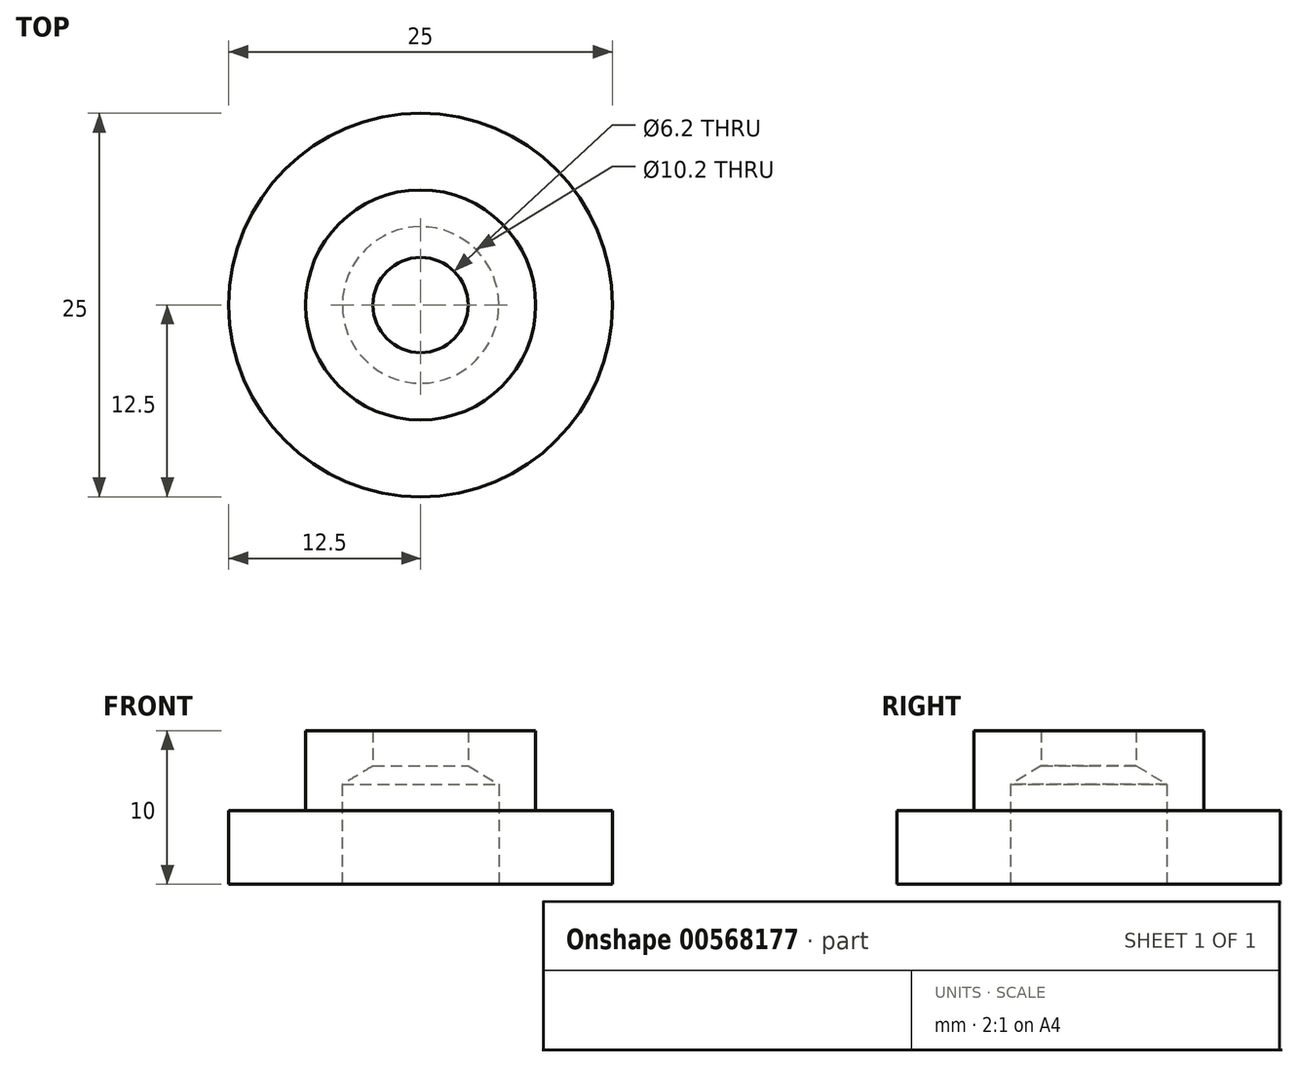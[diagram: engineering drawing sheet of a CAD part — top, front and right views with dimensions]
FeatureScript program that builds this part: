
annotation { "Feature Type Name" : "Feature", "Feature Type Description" : "" }
export const myFeature = defineFeature(function(context is Context, id is Id, definition is map)
    precondition{}
    {
        {
            var Q0;
            Q0=qCreatedBy(makeId("Top.planeOp"),FACE);
            var sketch = newSketch(context, id + "F0", { "sketchPlane" : qUnion([Q0])});
            skCircle(sketch, "E0", {"center": v(0, 0) * mm, "radius": 12.5 * mm});
            skCircle(sketch, "E1", {"center": v(0, 0) * mm, "radius": 7.5 * mm});
            skSolve(sketch);
        }
        {
            var Q0;
            Q0=makeQuery(id+"F0.imprint","IMPRINT",FACE,{"disambiguationData":[TD([[makeQuery(id+"F0.imprint","IMPRINT",EDGE,{"derivedFrom":sQuery(id+"F0.wireOp",EDGE,"E1")}),1.0]])]});
            extrude(context, id + "F1", {"entities" : qUnion([Q0]), "depth" : 10 * mm, "offsetDistance" : 25 * mm});
        }
        {
            var Q0;
            Q0=makeQuery(id+"F0.imprint","IMPRINT",FACE,{"disambiguationData":[TD([[makeQuery(id+"F0.imprint","IMPRINT",EDGE,{"derivedFrom":sQuery(id+"F0.wireOp",EDGE,"E0")}),1.0]])]});
            extrude(context, id + "F2", {"entities" : qUnion([Q0]), "operationType" : NewBodyOperationType.ADD, "depth" : 4.8 * mm, "offsetDistance" : 25 * mm});
        }
        {
            var Q0;
            Q0=sQuery(id+"F0.wireOp",VERTEX,"E0.center");
            var Q1;
            Q1=makeQuery(id+"F1.opExtrude","SWEPT_BODY",BODY,{"disambiguationData":[OSD([sQuery(id+"F0.wireOp",EDGE,"E1")])]});
            hole(context, id + "F3", {"style" : HoleStyle.SIMPLE, "endStyle" : HoleEndStyle.BLIND, "oppositeDirection" : true, "holeDiameter" : 6.2 * mm, "holeDepth" : 10 * mm, "isTappedThrough" : true, "tappedDepth" : 12 * mm, "tapClearance" : 3, "locations" : qUnion([Q0]), "scope" : qUnion([Q1])});
        }
        {
            var Q0;
            Q0=sQuery(id+"F0.wireOp",VERTEX,"E0.center");
            var Q1;
            Q1=makeQuery(id+"F1.opExtrude","SWEPT_BODY",BODY,{"disambiguationData":[OSD([sQuery(id+"F0.wireOp",EDGE,"E1")])]});
            hole(context, id + "F4", {"style" : HoleStyle.SIMPLE, "endStyle" : HoleEndStyle.BLIND, "oppositeDirection" : true, "holeDiameter" : 10.2 * mm, "holeDepth" : 6.5 * mm, "isTappedThrough" : true, "tappedDepth" : 12 * mm, "tapClearance" : 3, "locations" : qUnion([Q0]), "scope" : qUnion([Q1])});
        }
    });
